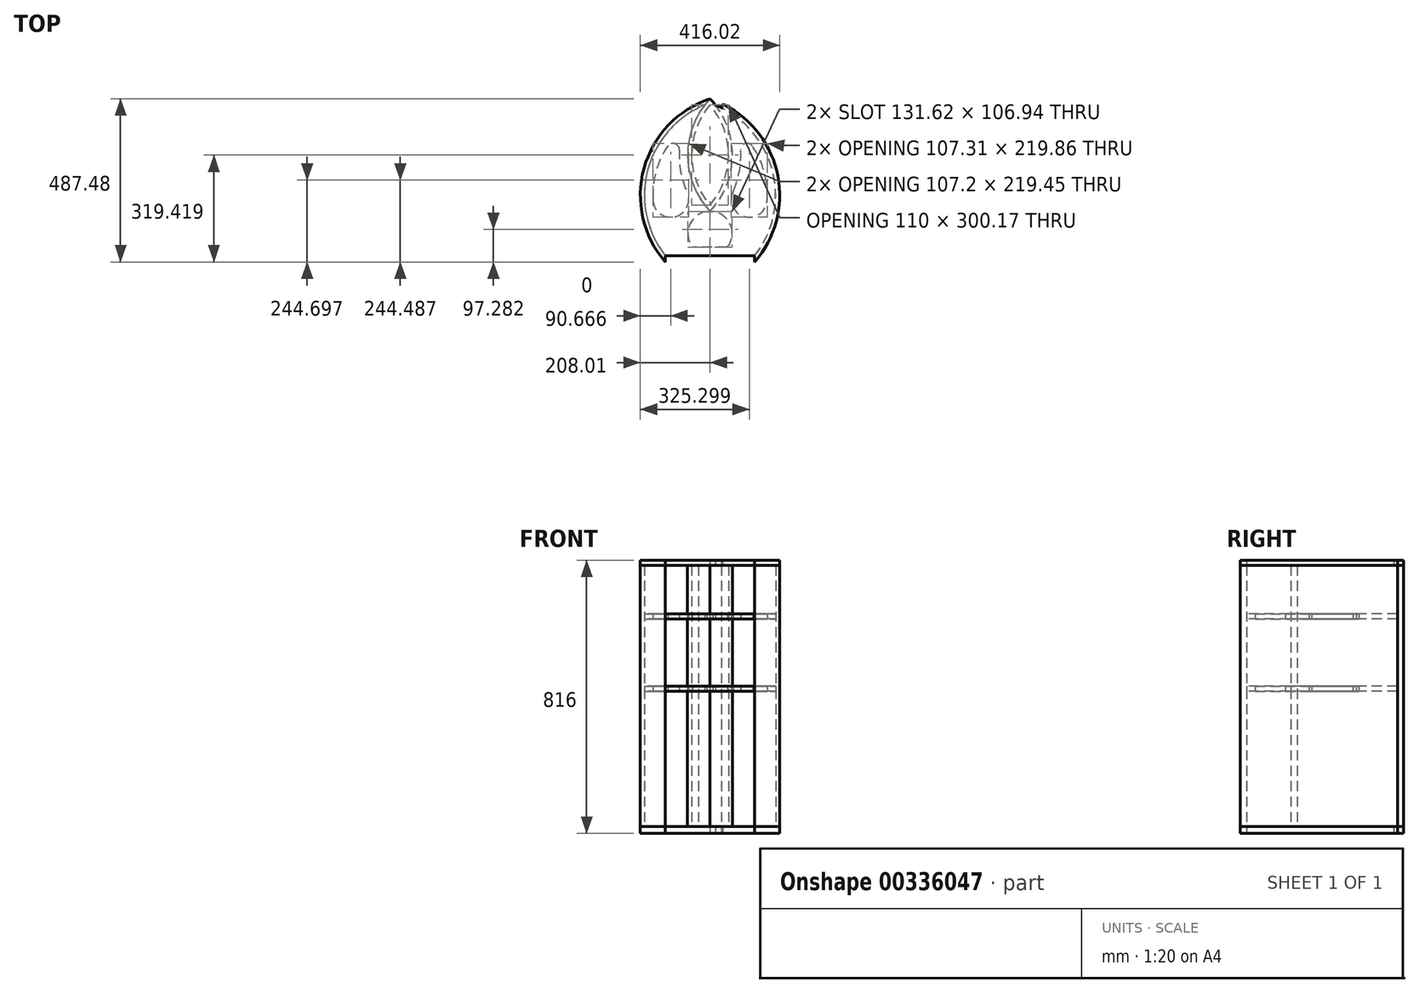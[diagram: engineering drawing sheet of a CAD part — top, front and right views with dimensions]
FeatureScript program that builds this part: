
annotation { "Feature Type Name" : "Feature", "Feature Type Description" : "" }
export const myFeature = defineFeature(function(context is Context, id is Id, definition is map)
    precondition{}
    {
        {
            var Q0;
            Q0=qCreatedBy(makeId("Top.planeOp"),FACE);
            var sketch = newSketch(context, id + "F0", { "sketchPlane" : qUnion([Q0])});
            skPoint(sketch, "E0.middle", {"position": v(0, 0) * mm});
            skPoint(sketch, "E1.middle", {"position": v(0, 107.37) * mm});
            skArc(sketch, "E2", {"start": v(-16.09, 269.38) * mm, "mid": v(-186.57, 73.6) * mm, "end": v(-133.43, -180.5) * mm});
            skArc(sketch, "E3", {"start": v(133.43, -180.5) * mm, "mid": v(186.57, 73.6) * mm, "end": v(16.09, 269.38) * mm});
            skArc(sketch, "E4", {"start": v(0, 288.17) * mm, "mid": v(-67, 120.1) * mm, "end": v(0, -47.95) * mm});
            skArc(sketch, "E5", {"start": v(0, -47.95) * mm, "mid": v(67, 120.1) * mm, "end": v(0, 288.17) * mm});
            skLineSegment(sketch, "E6", {"start": v(133.43, -180.5) * mm, "end": v(-133.43, -180.5) * mm});
            skPoint(sketch, "E7.orphan", {"position": v(0, -275.5) * mm});
            skArc(sketch, "E8.0", {"start": v(0, 288.17) * mm, "mid": v(-197.24, 80.16) * mm, "end": v(-133.43, -199.3) * mm});
            skArc(sketch, "E8.1", {"start": v(133.43, -199.3) * mm, "mid": v(197.24, 80.16) * mm, "end": v(0, 288.17) * mm});
            skArc(sketch, "E9.0", {"start": v(0, 270.2) * mm, "mid": v(-55, 120.1) * mm, "end": v(0, -29.98) * mm});
            skArc(sketch, "E9.1", {"start": v(0, -29.98) * mm, "mid": v(55, 120.1) * mm, "end": v(0, 270.2) * mm});
            skLineSegment(sketch, "E10", {"start": v(-133.43, -180.5) * mm, "end": v(-133.43, -199.3) * mm});
            skLineSegment(sketch, "E11", {"start": v(133.43, -180.5) * mm, "end": v(133.43, -199.3) * mm});
            skArc(sketch, "E12", {"start": v(-37.53, 259.45) * mm, "mid": v(-34.93, 267.53) * mm, "end": v(-43, 270.13) * mm});
            skArc(sketch, "E13.MirrorCS", {"start": v(37.53, 259.45) * mm, "mid": v(34.93, 267.53) * mm, "end": v(43, 270.13) * mm});
            skArc(sketch, "E14.1", {"start": v(170.56, -15.53) * mm, "mid": v(161.75, 69.64) * mm, "end": v(126.4, 147.63) * mm});
            skLineSegment(sketch, "E14.2", {"start": v(51.85, -155.5) * mm, "end": v(-51.85, -155.5) * mm});
            skArc(sketch, "E15.trimOffspring", {"start": v(-126.4, 147.63) * mm, "mid": v(-161.75, 69.64) * mm, "end": v(-170.56, -15.53) * mm});
            skArc(sketch, "E16", {"start": v(51.85, -155.5) * mm, "mid": v(61.5, -89.53) * mm, "end": v(8.9, -48.55) * mm});
            skArc(sketch, "E17.trimOffspring", {"start": v(-91.46, 137.12) * mm, "mid": v(-87.32, 70.1) * mm, "end": v(-66.71, 6.19) * mm});
            skArc(sketch, "E18", {"start": v(-170.56, -15.53) * mm, "mid": v(-106.16, -64.34) * mm, "end": v(-66.71, 6.19) * mm});
            skArc(sketch, "E19", {"start": v(-91.46, 137.12) * mm, "mid": v(-105.36, 154.28) * mm, "end": v(-126.4, 147.63) * mm});
            skArc(sketch, "E20.MirrorCS", {"start": v(170.56, -15.53) * mm, "mid": v(102.17, -63.34) * mm, "end": v(70.08, 13.69) * mm});
            skArc(sketch, "E21.MirrorCS", {"start": v(91.46, 137.12) * mm, "mid": v(105.36, 154.28) * mm, "end": v(126.4, 147.63) * mm});
            skPoint(sketch, "E22.orphan", {"position": v(0, -180.5) * mm});
            skLineSegment(sketch, "E23", {"start": v(-8.9, -48.55) * mm, "end": v(8.9, -48.55) * mm});
            skArc(sketch, "E24.trimOffspring", {"start": v(-8.9, -48.55) * mm, "mid": v(-61.5, -89.53) * mm, "end": v(-51.85, -155.5) * mm});
            skArc(sketch, "E25.trimOffspring", {"start": v(70.08, 13.69) * mm, "mid": v(88.05, 74.14) * mm, "end": v(91.46, 137.12) * mm});
            skSolve(sketch);
        }
        {
            var Q0;
            {var subQ3=sQuery(id+"F0.wireOp",EDGE,"E12");Q0=makeQuery(id+"F0.imprint","IMPRINT",FACE,{"disambiguationData":[TD([[makeQuery(id+"F0.imprint","IMPRINT",EDGE,{"derivedFrom":subQ3}),-1.0]])]});}
            var Q1;
            {var subQ3=sQuery(id+"F0.wireOp",EDGE,"E13.MirrorCS");Q1=makeQuery(id+"F0.imprint","IMPRINT",FACE,{"disambiguationData":[TD([[makeQuery(id+"F0.imprint","IMPRINT",EDGE,{"derivedFrom":subQ3}),1.0]])]});}
            var Q2;
            Q2=makeQuery(id+"F0.imprint","IMPRINT",FACE,{"disambiguationData":[TD([[makeQuery(id+"F0.imprint","IMPRINT",EDGE,{"derivedFrom":sQuery(id+"F0.wireOp",EDGE,"E9.0")}),-1.0]])]});
            var Q3;
            {var subQ4=sQuery(id+"F0.wireOp",EDGE,"E6");Q3=makeQuery(id+"F0.imprint","IMPRINT",FACE,{"disambiguationData":[TD([[makeQuery(id+"F0.imprint","IMPRINT",EDGE,{"derivedFrom":subQ4}),-1.0]])]});}
            var Q4;
            {var subQ0=sQuery(id+"F0.wireOp",EDGE,"E10");Q4=makeQuery(id+"F0.imprint","IMPRINT",FACE,{"disambiguationData":[TD([[makeQuery(id+"F0.imprint","IMPRINT",EDGE,{"derivedFrom":subQ0}),-1.0]])]});}
            var Q5;
            {var subQ0=sQuery(id+"F0.wireOp",EDGE,"E11");Q5=makeQuery(id+"F0.imprint","IMPRINT",FACE,{"disambiguationData":[TD([[makeQuery(id+"F0.imprint","IMPRINT",EDGE,{"derivedFrom":subQ0}),1.0]])]});}
            var Q6;
            {var subQ0=sQuery(id+"F0.wireOp",EDGE,"E17.trimOffspring");Q6=makeQuery(id+"F0.imprint","IMPRINT",FACE,{"disambiguationData":[TD([[makeQuery(id+"F0.imprint","IMPRINT",EDGE,{"derivedFrom":subQ0}),-1.0]])]});}
            var Q7;
            Q7=makeQuery(id+"F0.imprint","IMPRINT",FACE,{"disambiguationData":[TD([[makeQuery(id+"F0.imprint","IMPRINT",EDGE,{"derivedFrom":sQuery(id+"F0.wireOp",EDGE,"E9.0")}),1.0]])]});
            var Q8;
            Q8=makeQuery(id+"F0.imprint","IMPRINT",FACE,{"disambiguationData":[TD([[makeQuery(id+"F0.imprint","IMPRINT",EDGE,{"derivedFrom":sQuery(id+"F0.wireOp",EDGE,"E14.1")}),1.0]])]});
            var Q9;
            Q9=makeQuery(id+"F0.imprint","IMPRINT",FACE,{"disambiguationData":[TD([[makeQuery(id+"F0.imprint","IMPRINT",EDGE,{"derivedFrom":sQuery(id+"F0.wireOp",EDGE,"E14.2")}),-1.0]])]});
            extrude(context, id + "F1", {"entities" : qUnion([Q0, Q1, Q2, Q3, Q4, Q5, Q6, Q7, Q8, Q9]), "depth" : 20 * mm});
        }
        {
            var Q0;
            {var subQ4=sQuery(id+"F0.wireOp",EDGE,"E6");Q0=makeQuery(id+"F0.imprint","IMPRINT",FACE,{"disambiguationData":[TD([[makeQuery(id+"F0.imprint","IMPRINT",EDGE,{"derivedFrom":subQ4}),-1.0]])]});}
            extrude(context, id + "F2", {"entities" : qUnion([Q0]), "operationType" : NewBodyOperationType.ADD, "depth" : 440 * mm, "hasSecondDirection" : true, "secondDirectionOppositeDirection" : false, "secondDirectionDepth" : 424 * mm});
        }
        {
            var Q0;
            {var subQ0=sQuery(id+"F0.wireOp",EDGE,"E10");Q0=makeQuery(id+"F0.imprint","IMPRINT",FACE,{"disambiguationData":[TD([[makeQuery(id+"F0.imprint","IMPRINT",EDGE,{"derivedFrom":subQ0}),-1.0]])]});}
            var Q1;
            Q1=makeQuery(id+"F0.imprint","IMPRINT",FACE,{"disambiguationData":[TD([[makeQuery(id+"F0.imprint","IMPRINT",EDGE,{"derivedFrom":sQuery(id+"F0.wireOp",EDGE,"E9.0")}),-1.0]])]});
            var Q2;
            {var subQ0=sQuery(id+"F0.wireOp",EDGE,"E11");Q2=makeQuery(id+"F0.imprint","IMPRINT",FACE,{"disambiguationData":[TD([[makeQuery(id+"F0.imprint","IMPRINT",EDGE,{"derivedFrom":subQ0}),1.0]])]});}
            extrude(context, id + "F3", {"entities" : qUnion([Q0, Q1, Q2]), "depth" : 800 * mm, "hasSecondDirection" : true, "secondDirectionOppositeDirection" : false, "secondDirectionDepth" : 20 * mm});
        }
        {
            var Q0;
            {var subQ4=sQuery(id+"F0.wireOp",EDGE,"E6");Q0=makeQuery(id+"F0.imprint","IMPRINT",FACE,{"disambiguationData":[TD([[makeQuery(id+"F0.imprint","IMPRINT",EDGE,{"derivedFrom":subQ4}),-1.0]])]});}
            extrude(context, id + "F4", {"entities" : qUnion([Q0]), "depth" : 656 * mm, "hasSecondDirection" : true, "secondDirectionOppositeDirection" : false, "secondDirectionDepth" : 640 * mm});
        }
        {
            var Q0;
            {var subQ0=sQuery(id+"F0.wireOp",EDGE,"E10");Q0=makeQuery(id+"F0.imprint","IMPRINT",FACE,{"disambiguationData":[TD([[makeQuery(id+"F0.imprint","IMPRINT",EDGE,{"derivedFrom":subQ0}),-1.0]])]});}
            var Q1;
            {var subQ4=sQuery(id+"F0.wireOp",EDGE,"E6");Q1=makeQuery(id+"F0.imprint","IMPRINT",FACE,{"disambiguationData":[TD([[makeQuery(id+"F0.imprint","IMPRINT",EDGE,{"derivedFrom":subQ4}),-1.0]])]});}
            var Q2;
            {var subQ0=sQuery(id+"F0.wireOp",EDGE,"E17.trimOffspring");Q2=makeQuery(id+"F0.imprint","IMPRINT",FACE,{"disambiguationData":[TD([[makeQuery(id+"F0.imprint","IMPRINT",EDGE,{"derivedFrom":subQ0}),-1.0]])]});}
            var Q3;
            Q3=makeQuery(id+"F0.imprint","IMPRINT",FACE,{"disambiguationData":[TD([[makeQuery(id+"F0.imprint","IMPRINT",EDGE,{"derivedFrom":sQuery(id+"F0.wireOp",EDGE,"E9.0")}),1.0]])]});
            var Q4;
            Q4=makeQuery(id+"F0.imprint","IMPRINT",FACE,{"disambiguationData":[TD([[makeQuery(id+"F0.imprint","IMPRINT",EDGE,{"derivedFrom":sQuery(id+"F0.wireOp",EDGE,"E9.0")}),-1.0]])]});
            var Q5;
            Q5=makeQuery(id+"F0.imprint","IMPRINT",FACE,{"disambiguationData":[TD([[makeQuery(id+"F0.imprint","IMPRINT",EDGE,{"derivedFrom":sQuery(id+"F0.wireOp",EDGE,"E14.2")}),-1.0]])]});
            var Q6;
            Q6=makeQuery(id+"F0.imprint","IMPRINT",FACE,{"disambiguationData":[TD([[makeQuery(id+"F0.imprint","IMPRINT",EDGE,{"derivedFrom":sQuery(id+"F0.wireOp",EDGE,"E14.1")}),1.0]])]});
            var Q7;
            {var subQ0=sQuery(id+"F0.wireOp",EDGE,"E11");Q7=makeQuery(id+"F0.imprint","IMPRINT",FACE,{"disambiguationData":[TD([[makeQuery(id+"F0.imprint","IMPRINT",EDGE,{"derivedFrom":subQ0}),1.0]])]});}
            var Q8;
            {var subQ3=sQuery(id+"F0.wireOp",EDGE,"E12");Q8=makeQuery(id+"F0.imprint","IMPRINT",FACE,{"disambiguationData":[TD([[makeQuery(id+"F0.imprint","IMPRINT",EDGE,{"derivedFrom":subQ3}),-1.0]])]});}
            var Q9;
            {var subQ3=sQuery(id+"F0.wireOp",EDGE,"E13.MirrorCS");Q9=makeQuery(id+"F0.imprint","IMPRINT",FACE,{"disambiguationData":[TD([[makeQuery(id+"F0.imprint","IMPRINT",EDGE,{"derivedFrom":subQ3}),1.0]])]});}
            extrude(context, id + "F5", {"entities" : qUnion([Q0, Q1, Q2, Q3, Q4, Q5, Q6, Q7, Q8, Q9]), "depth" : 816 * mm, "hasSecondDirection" : true, "secondDirectionOppositeDirection" : false, "secondDirectionDepth" : 800 * mm});
        }
    });
